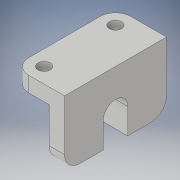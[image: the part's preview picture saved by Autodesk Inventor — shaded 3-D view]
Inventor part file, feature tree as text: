
AUTODESK INVENTOR PART (.ipt)
format: ipt  version: 2019 (Build 230136000, 136)  size: 187,392 bytes
history: native  units: mm
features: extrude x7, sketch x7, projected_geometry x2, chamfer x1, fillet x1
ambient origin geometry x8: Origin, YZ Plane, XZ Plane, XY Plane, X Axis, Y Axis, Z Axis, Center Point
bodies: Solid1 (feature_tree)
feature tree (18):
  extrude  "Extrusion1"  Depth=100.0mm
  extrude  "Extrusion2"  Depth=24.0mm
  extrude  "Extrusion3"  Depth=65.0mm TaperAngle=0.0deg
  extrude  "Extrusion4"  Depth=30.0mm
  extrude  "Extrusion5"  Depth=50.0mm TaperAngle=0.0deg
  extrude  "Extrusion6"  Depth=40.0mm
  chamfer  "Chamfer1"  Distance=4.0mm
  fillet  "Fillet1"  Radius=10.0mm
  extrude  "Extrusion7"  Depth=15.0mm
  sketch  "Sketch1"  dims[d0=50.0mm d1=100.0mm]
  sketch  "Sketch2"  dims[d2=65.0mm d3=0.0mm d5=24.0mm]
  sketch  "Sketch3"  dims[d6=65.0mm d7=0.0mm d8=65.0mm d9=0.0mm]
  projected_geometry  "Projected Loop1"
  sketch  "Sketch4"  dims[d10=35.0mm d11=30.0mm]
  sketch  "Sketch5"  dims[d12=30.0mm d13=50.0mm d14=0.0mm]
  projected_geometry  "Projected Loop2"
  sketch  "Sketch6"  dims[d15=40.0mm d16=40.0mm d17=4.0mm d18=0.0mm d19=10.0mm]
  sketch  "Sketch7"  dims[d20=15.0mm d21=15.0mm d22=4.0mm d23=0.0mm d24=15.0mm d25=2.0mm d26=45.0deg d27=15.0mm d28=12.0mm d29=12.0mm d30=15.0mm d31=15.0mm d32=15.0mm d33=15.0mm d34=4.0mm d35=0.0mm]
